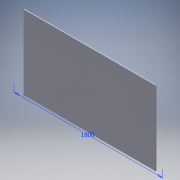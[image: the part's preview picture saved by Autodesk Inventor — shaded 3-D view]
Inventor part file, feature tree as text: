
AUTODESK INVENTOR PART (.ipt)
format: ipt  version: 2019 (Build 230136000, 136)  size: 98,304 bytes
history: native  units: mm
features: extrude x1, sketch x1
ambient origin geometry x8: Origin, YZ Plane, XZ Plane, XY Plane, X Axis, Y Axis, Z Axis, Center Point
bodies: Solid1 (feature_tree)
feature tree (2):
  extrude  "Extrusion1"  Depth=900.0mm
  sketch  "Sketch1"  dims[d0=1800.0mm d1=900.0mm d2=10.0mm d3=0.0mm]
